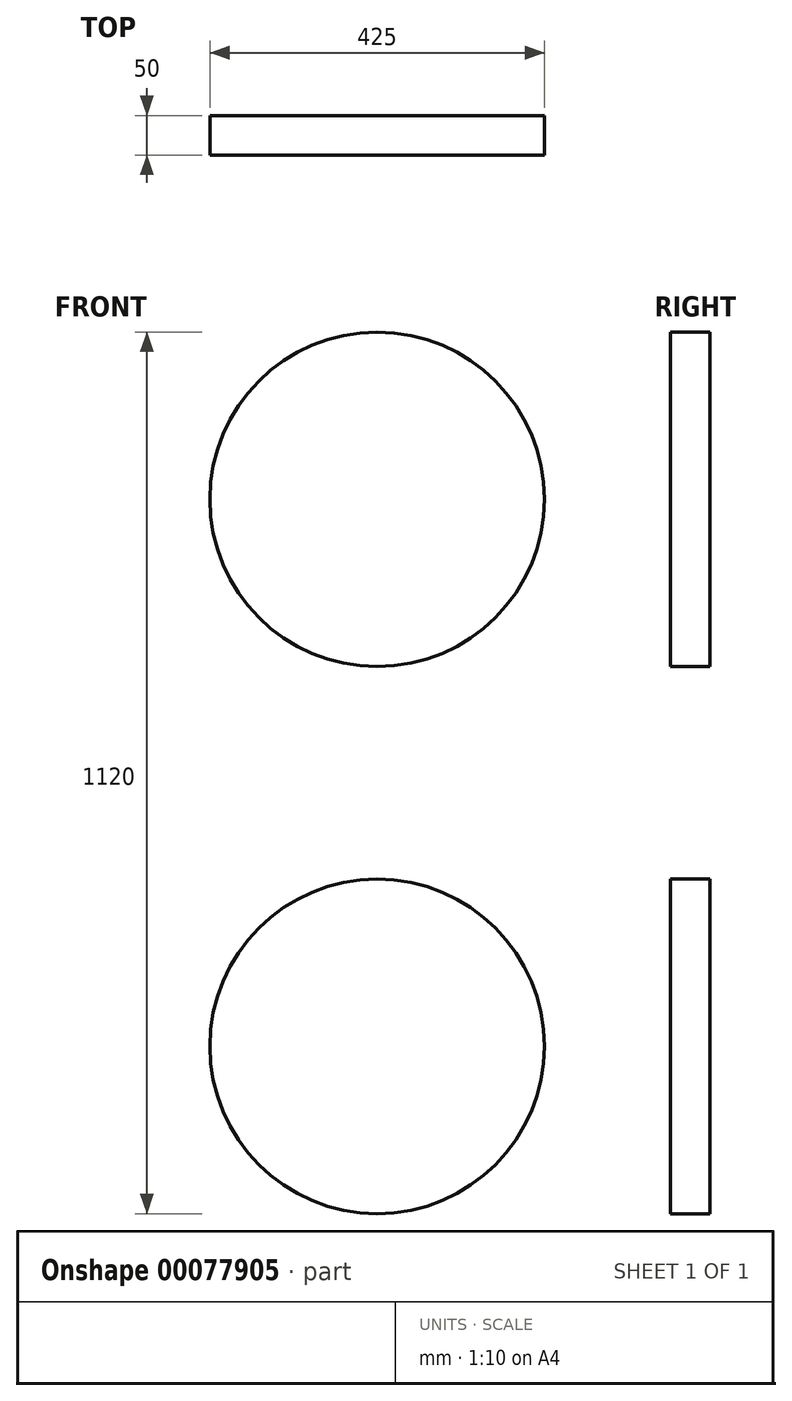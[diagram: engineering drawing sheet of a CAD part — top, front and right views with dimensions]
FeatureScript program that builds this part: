
annotation { "Feature Type Name" : "Feature", "Feature Type Description" : "" }
export const myFeature = defineFeature(function(context is Context, id is Id, definition is map)
    precondition{}
    {
        {
            var Q0;
            Q0=qCreatedBy(makeId("Front.planeOp"),FACE);
            var sketch = newSketch(context, id + "F0", { "sketchPlane" : qUnion([Q0])});
            skCircle(sketch, "E0", {"center": v(0, 347.5) * mm, "radius": 212.5 * mm});
            skCircle(sketch, "E1.MirrorC", {"center": v(0, -347.5) * mm, "radius": 212.5 * mm});
            skSolve(sketch);
        }
        {
            var Q0;
            Q0 = qSketchRegion(id + "F0", true);
            var Q1;
            Q1 = qConstructionFilter(qBodyType(qCreatedBy(id + "F0" ,EDGE), BodyType.WIRE), ConstructionObject.NO);
            extrude(context, id + "F1", {"entities" : qUnion([Q0]), "surfaceEntities" : qUnion([Q1]), "endBound" : BoundingType.SYMMETRIC, "depth" : 50 * mm});
        }
    });
